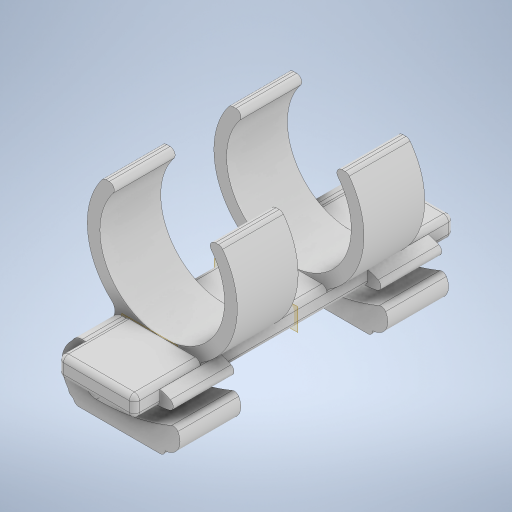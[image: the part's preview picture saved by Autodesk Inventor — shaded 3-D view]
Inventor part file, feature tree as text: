
AUTODESK INVENTOR PART (.ipt)
format: ipt  version: 2024 (Build 280153000, 153)  size: 442,880 bytes
history: native  units: mm
features: fillet x4, extrude x3, plane x3, sketch x3, mirror x2
ambient origin geometry x8: Origin, YZ Plane, XZ Plane, XY Plane, X Axis, Y Axis, Z Axis, Center Point
bodies: Solid1 (feature_tree)
feature tree (15):
  extrude  "Extrusion1"  Depth=63.0mm
  plane  "Work Plane5"
  extrude  "Extrusion4"  [1 undecoded]
  plane  "Work Plane6"
  mirror  "Mirror4"
  fillet  "Fillet6"  Radius=29.6mm
  plane  "Work Plane7"
  extrude  "Extrusion6"  Depth=12.0mm TaperAngle=0.0deg
  mirror  "Mirror6"
  fillet  "Fillet7"  [1 undecoded]
  fillet  "Fillet8"  Radius=1.0mm
  fillet  "Fillet9"  [1 undecoded]
  sketch  "Sketch1"  dims[d0=15.0mm d1=63.0mm]
  sketch  "Sketch5"  dims[d3=4.0mm d4=0.0mm d28=-13.0mm d30=29.6mm]
  sketch  "Sketch6"  dims[d32=1.0mm d33=12.0mm d34=0.0mm d35=-31.5mm d36=1.0mm d37=-5.0mm d42=1.0mm d43=1.0mm d44=12.0mm d45=0.0mm d46=2.0mm d47=2.0mm d48=2.0mm d49=1.0mm d50=1.0mm]
note: 3 required parameter values undecoded (feature->parameter linkage not recoverable at this tier; creation-order binding heuristic only, values carry confidence <= 0.55)
